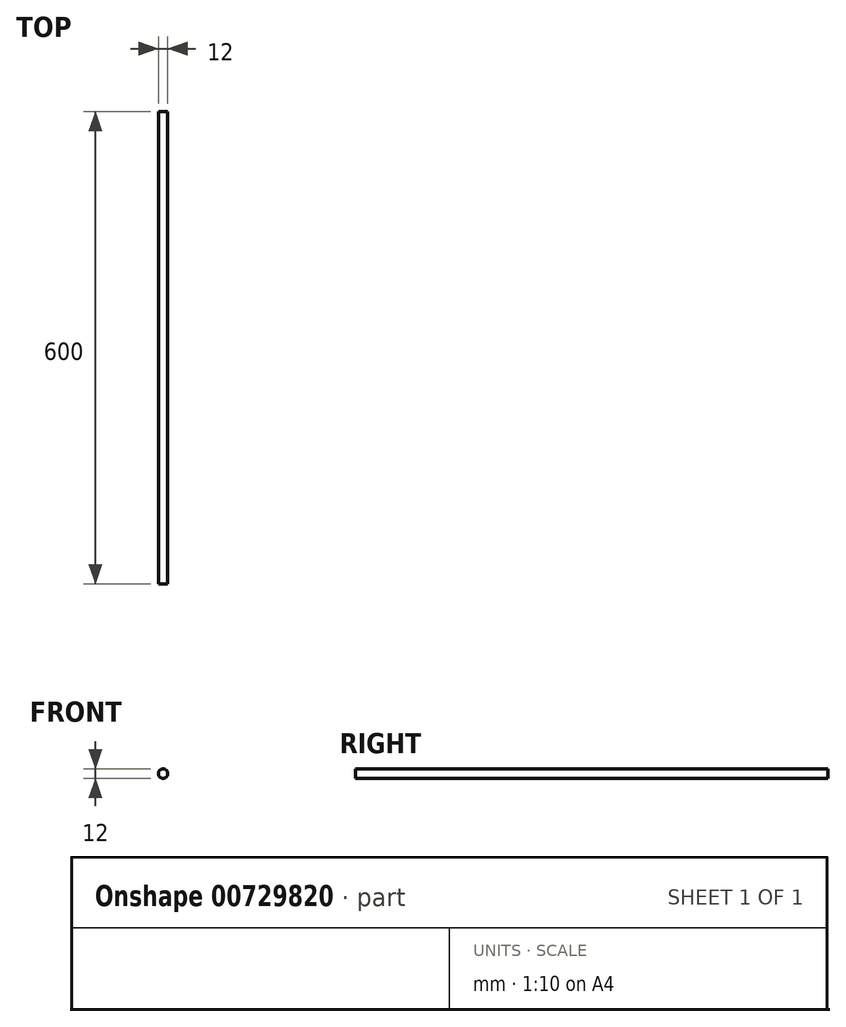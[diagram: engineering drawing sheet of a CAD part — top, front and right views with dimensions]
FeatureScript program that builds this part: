
annotation { "Feature Type Name" : "Feature", "Feature Type Description" : "" }
export const myFeature = defineFeature(function(context is Context, id is Id, definition is map)
    precondition{}
    {
        {
            var Q0;
            Q0=qCreatedBy(makeId("Front.planeOp"),FACE);
            var sketch = newSketch(context, id + "F0", { "sketchPlane" : qUnion([Q0])});
            skCircle(sketch, "E0", {"center": v(0, 0) * mm, "radius": 6 * mm});
            skSolve(sketch);
        }
        {
            var Q0;
            Q0=qSketchRegion(id+"F0",true);
            extrude(context, id + "F1", {"entities" : qUnion([Q0]), "depth" : 600 * mm, "offsetDistance" : 25 * mm});
        }
    });
